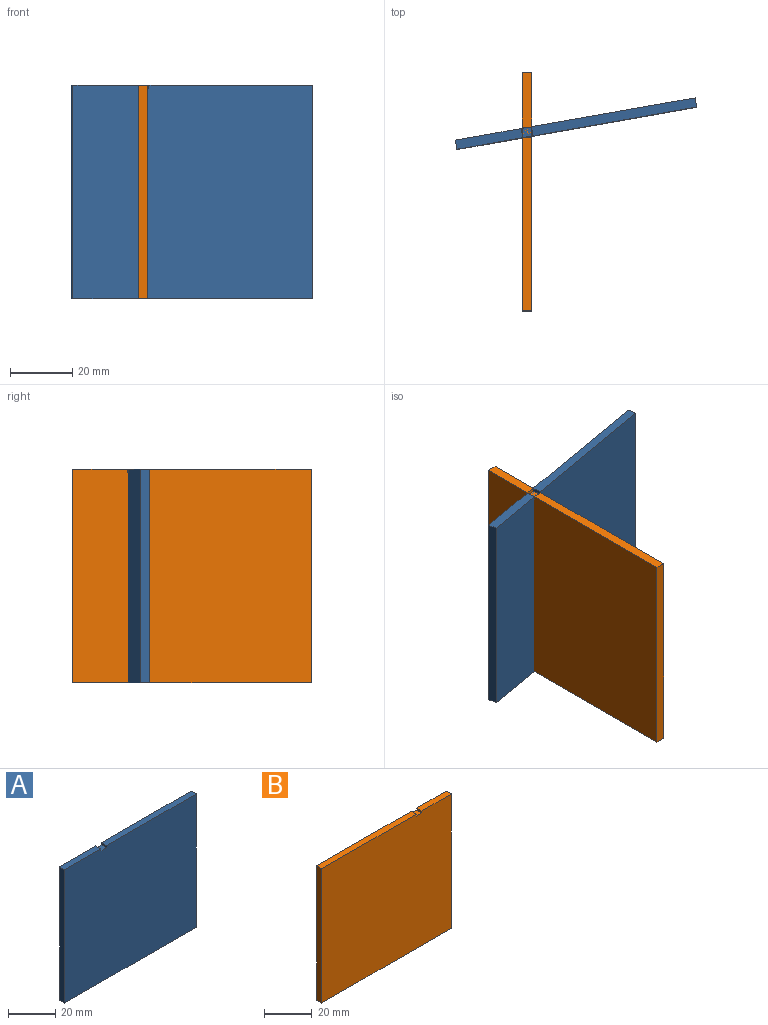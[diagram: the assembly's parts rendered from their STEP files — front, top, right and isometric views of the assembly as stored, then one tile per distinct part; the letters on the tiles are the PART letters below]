
ASSEMBLY  parts=2 mates=1
PART A: 10 faces, bbox 78.3x3x68.8 mm
  f0: plane 53.48x3mm, normal (0,0,1), area 160.4mm2, adj f1,f5,f6,f8
  f1: plane 78.33x68.78mm, normal (0,-1,0), area 5384.4mm2, adj f0,f2,f3,f4,f5,f7,f8,f9
  f2: plane 21.55x3mm, normal (0,0,1), area 64.6mm2, adj f1,f3,f6,f7
  f3: plane 68.78x3mm, normal (-1,0,0), area 206.4mm2, adj f1,f2,f4,f6
  f4: plane 78.33x3mm, normal (0,0,-1), area 235mm2, adj f1,f3,f5,f6
  f5: plane 68.78x3mm, normal (1,0,0), area 206.4mm2, adj f0,f1,f4,f6
  f6: plane 78.33x68.78mm, normal (0,1,0), area 5384.4mm2, adj f0,f2,f3,f4,f5,f7,f8,f9
  f7: plane 3x1mm, normal (1,0,0), area 3mm2, adj f1,f2,f6,f9
  f8: plane 3x1mm, normal (-1,0,0), area 3mm2, adj f0,f1,f6,f9
  f9: plane 3.3x3mm, normal (0,0,1), area 9.9mm2, adj f1,f6,f7,f8
PART B: 10 faces, bbox 76.7x3x68.8 mm
  f0: plane 55.87x3mm, normal (0,0,1), area 167.6mm2, adj f1,f4,f6,f8
  f1: plane 76.66x68.78mm, normal (0,-1,0), area 5269.9mm2, adj f0,f2,f3,f4,f5,f7,f8,f9
  f2: plane 68.78x3mm, normal (1,0,0), area 206.4mm2, adj f1,f3,f5,f6
  f3: plane 17.5x3mm, normal (0,0,1), area 52.5mm2, adj f1,f2,f6,f7
  f4: plane 68.78x3mm, normal (-1,0,0), area 206.4mm2, adj f0,f1,f5,f6
  f5: plane 76.66x3mm, normal (0,0,-1), area 230mm2, adj f1,f2,f4,f6
  f6: plane 76.66x68.78mm, normal (0,1,0), area 5269.9mm2, adj f0,f2,f3,f4,f5,f7,f8,f9
  f7: plane 3x1mm, normal (-1,0,0), area 3mm2, adj f1,f3,f6,f9
  f8: plane 3x1mm, normal (1,0,0), area 3mm2, adj f0,f1,f6,f9
  f9: plane 3.3x3mm, normal (0,0,1), area 9.9mm2, adj f1,f6,f7,f8
PLACE A rot(axis=(0,0,1),10deg) t=(-14.66,-7.46,-0.68)mm
PLACE B rot(axis=(0,0,1),90deg) t=(-4.25,37.09,-0.68)mm
MATE revolute A.f9 <-> B.f9  axis (0,0,1) through (-2.75,-6.89,17.41)mm
